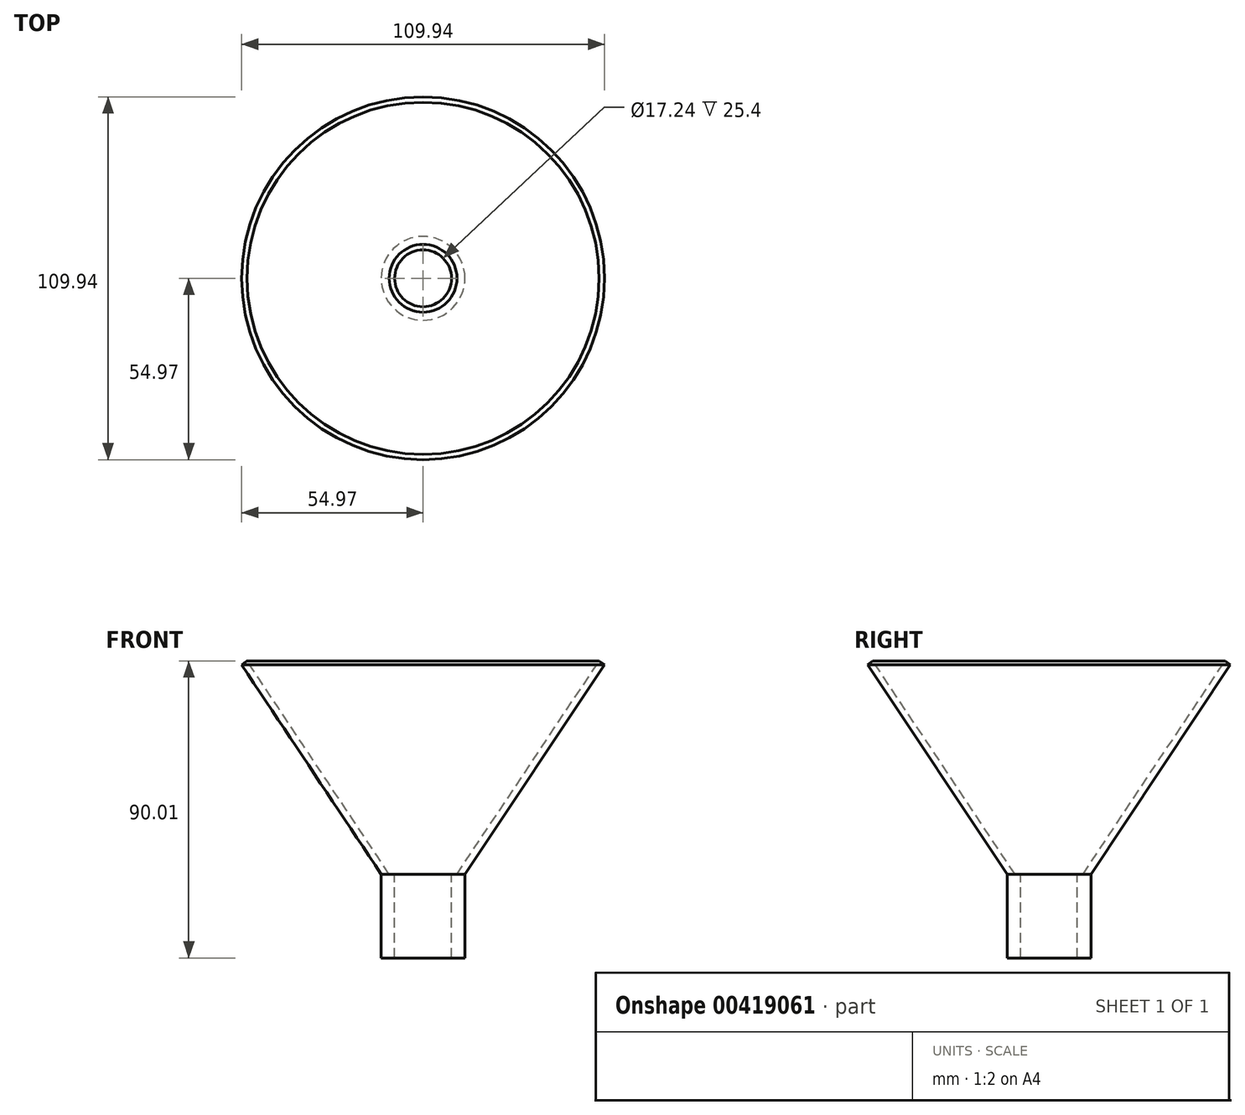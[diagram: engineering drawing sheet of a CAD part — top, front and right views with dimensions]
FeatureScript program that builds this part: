
annotation { "Feature Type Name" : "Feature", "Feature Type Description" : "" }
export const myFeature = defineFeature(function(context is Context, id is Id, definition is map)
    precondition{}
    {
        {
            var Q0;
            Q0=qCreatedBy(makeId("Front.planeOp"),FACE);
            var sketch = newSketch(context, id + "F0", { "sketchPlane" : qUnion([Q0])});
            skLineSegment(sketch, "E0", {"start": v(0, 0) * mm, "end": v(42.27, 63.4) * mm});
            skLineSegment(sketch, "E1", {"start": v(0, 0) * mm, "end": v(0, -25.4) * mm});
            skLineSegment(sketch, "E2", {"start": v(0, -25.4) * mm, "end": v(-12.7, -25.4) * mm});
            skLineSegment(sketch, "E3", {"start": v(-12.7, -25.4) * mm, "end": v(-12.7, -20.81) * mm});
            skLineSegment(sketch, "E4", {"start": v(-12.7, -20.81) * mm, "end": v(-12.7, 0) * mm});
            skLineSegment(sketch, "E5", {"start": v(-12.7, 0) * mm, "end": v(-2.42, 0) * mm});
            skLineSegment(sketch, "E6", {"start": v(-2.42, 0) * mm, "end": v(40.65, 64.6) * mm});
            skLineSegment(sketch, "E7", {"start": v(40.65, 64.6) * mm, "end": v(42.27, 63.4) * mm});
            skSolve(sketch);
        }
        {
            var Q0;
            Q0=makeQuery(id+"F0.imprint","IMPRINT",FACE,{"disambiguationData":[TD([[makeQuery(id+"F0.imprint","IMPRINT",EDGE,{"derivedFrom":sQuery(id+"F0.wireOp",EDGE,"E0")}),1.0]])]});
            var Q1;
            Q1=sQuery(id+"F0.wireOp",EDGE,"E4");
            revolve(context, id + "F1", {"entities" : qUnion([Q0]), "axis" : qUnion([Q1]), "revolveType" : RevolveType.FULL});
        }
        {
            var Q0;
            Q0=makeQuery(id+"F1.opRevolve","SWEPT_FACE",FACE,{"disambiguationData":[OSD([sQuery(id+"F0.wireOp",EDGE,"E5")])]});
            var sketch = newSketch(context, id + "F2", { "sketchPlane" : qUnion([Q0])});
            skCircle(sketch, "E8", {"center": v(-12.7, 0) * mm, "radius": 8.62 * mm});
            skSolve(sketch);
        }
        {
            var Q0;
            Q0 = qSketchRegion(id + "F2", true);
            extrude(context, id + "F3", {"entities" : qUnion([Q0]), "operationType" : NewBodyOperationType.REMOVE, "oppositeDirection" : true, "depth" : 25.4 * mm});
        }
    });
